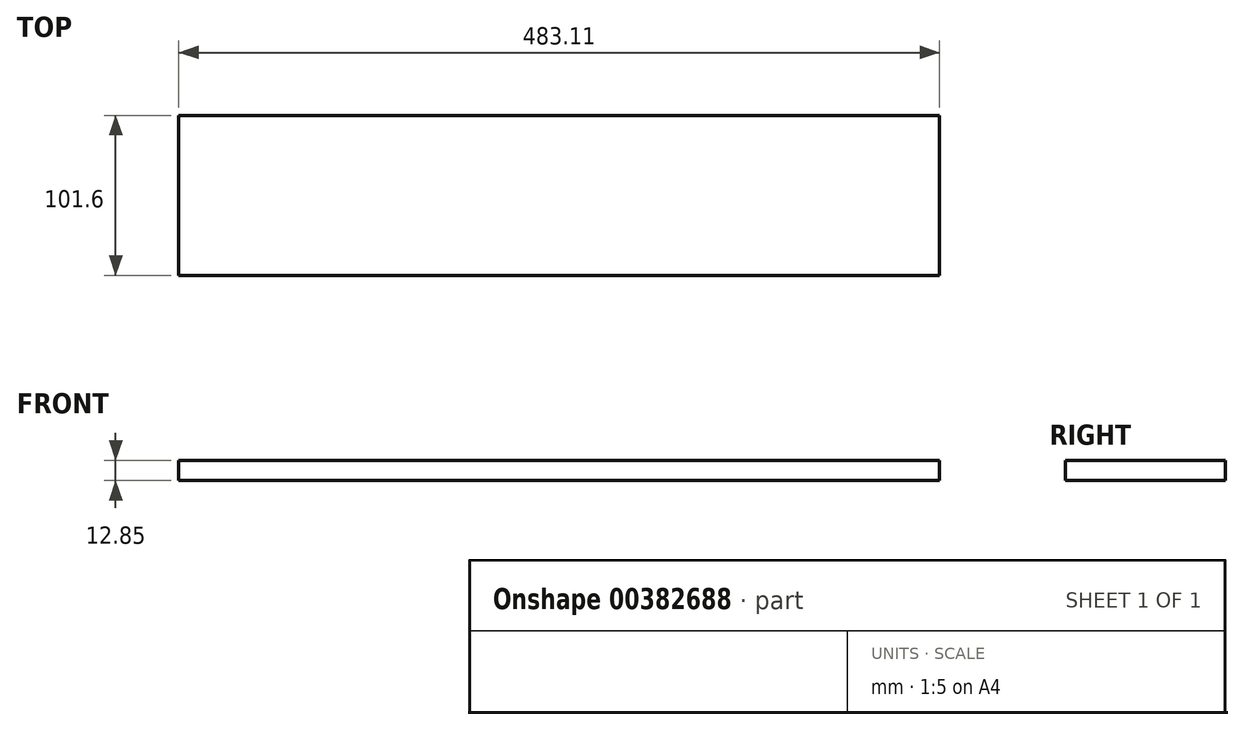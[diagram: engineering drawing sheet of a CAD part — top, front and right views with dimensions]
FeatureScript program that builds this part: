
annotation { "Feature Type Name" : "Feature", "Feature Type Description" : "" }
export const myFeature = defineFeature(function(context is Context, id is Id, definition is map)
    precondition{}
    {
        {
            var Q0;
            Q0=qCreatedBy(makeId("Top.planeOp"),FACE);
            var sketch = newSketch(context, id + "F0", { "sketchPlane" : qUnion([Q0])});
            skLineSegment(sketch, "E0.bottom", {"start": v(148.23, -59.95) * mm, "end": v(-334.88, -59.95) * mm});
            skLineSegment(sketch, "E0.top", {"start": v(148.23, 41.65) * mm, "end": v(-334.88, 41.65) * mm});
            skLineSegment(sketch, "E0.left", {"start": v(148.23, -59.95) * mm, "end": v(148.23, 41.65) * mm});
            skLineSegment(sketch, "E0.right", {"start": v(-334.88, -59.95) * mm, "end": v(-334.88, 41.65) * mm});
            skSolve(sketch);
        }
        {
            var Q0;
            Q0=makeQuery(id+"F0.imprint","IMPRINT",FACE,{"disambiguationData":[TD([[makeQuery(id+"F0.imprint","IMPRINT",EDGE,{"derivedFrom":sQuery(id+"F0.wireOp",EDGE,"E0.bottom")}),-1.0]])]});
            extrude(context, id + "F1", {"entities" : qUnion([Q0]), "depth" : 12.85 * mm});
        }
    });
